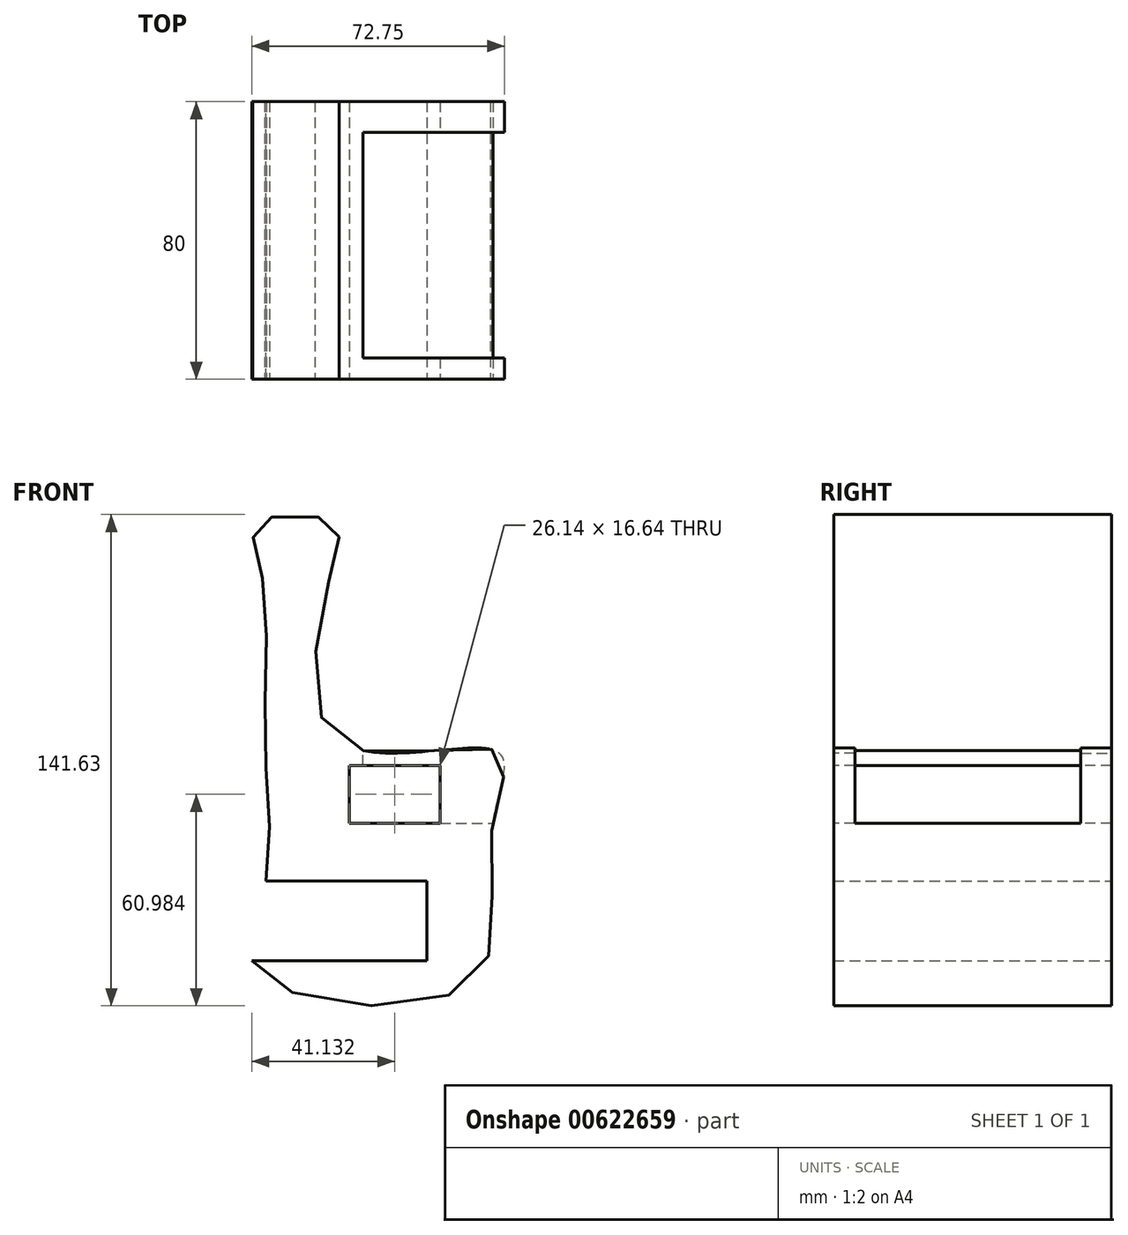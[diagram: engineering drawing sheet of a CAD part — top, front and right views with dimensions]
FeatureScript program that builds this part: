
annotation { "Feature Type Name" : "Feature", "Feature Type Description" : "" }
export const myFeature = defineFeature(function(context is Context, id is Id, definition is map)
    precondition{}
    {
        {
            var Q0;
            Q0=qCreatedBy(makeId("Front.planeOp"),FACE);
            var sketch = newSketch(context, id + "F0", { "sketchPlane" : qUnion([Q0])});
            skFitSpline(sketch, "E0", {"points": [v(-39.55, 48.72) * mm, v(-38.53, 0) * mm, v(-38.53, -41.59) * mm, v(-39.9, -67.05) * mm, v(20.54, -69.77) * mm, v(26.65, -27) * mm, v(28.35, -2.89) * mm, v(-17.14, 0) * mm, v(-19.52, 48.38) * mm, v(-19.52, 63.32) * mm, v(-40.57, 62.98) * mm, v(-39.55, 48.72) * mm]});
            skSolve(sketch);
        }
        {
            var Q0;
            Q0=makeQuery(id+"F0.imprint","IMPRINT",FACE,{"disambiguationData":[TD([[makeQuery(id+"F0.imprint","IMPRINT",EDGE,{"derivedFrom":sQuery(id+"F0.wireOp",EDGE,"E0")}),1.0]])]});
            extrude(context, id + "F1", {"entities" : qUnion([Q0]), "depth" : 80 * mm, "offsetDistance" : 25 * mm});
        }
        {
            var Q0;
            Q0=makeQuery(id+"F1.opExtrude","CAP_FACE",FACE,{"disambiguationData":[OSD([sQuery(id+"F0.wireOp",EDGE,"E0")])],"isStart":false});
            var sketch = newSketch(context, id + "F2", { "sketchPlane" : qUnion([Q0])});
            skLineSegment(sketch, "E1.bottom", {"start": v(-54.62, -40.25) * mm, "end": v(8.16, -40.25) * mm});
            skLineSegment(sketch, "E1.top", {"start": v(-54.62, -63.14) * mm, "end": v(8.16, -63.14) * mm});
            skLineSegment(sketch, "E1.left", {"start": v(-54.62, -40.25) * mm, "end": v(-54.62, -63.14) * mm});
            skLineSegment(sketch, "E1.right", {"start": v(8.16, -40.25) * mm, "end": v(8.16, -63.14) * mm});
            skSolve(sketch);
        }
        {
            var Q0;
            Q0 = qSketchRegion(id + "F2", true);
            extrude(context, id + "F3", {"entities" : qUnion([Q0]), "operationType" : NewBodyOperationType.REMOVE, "oppositeDirection" : true, "depth" : 80 * mm, "offsetDistance" : 25 * mm, "hasSecondDirection" : true, "secondDirectionOppositeDirection" : false, "secondDirectionDepth" : 25 * mm});
        }
        {
            var Q0;
            Q0=makeQuery(id+"F1.opExtrude","CAP_FACE",FACE,{"disambiguationData":[OSD([sQuery(id+"F0.wireOp",EDGE,"E0")])],"isStart":false});
            var sketch = newSketch(context, id + "F4", { "sketchPlane" : qUnion([Q0])});
            skLineSegment(sketch, "E2.bottom", {"start": v(-14.25, -6.89) * mm, "end": v(11.9, -6.89) * mm});
            skLineSegment(sketch, "E2.top", {"start": v(-14.25, -23.52) * mm, "end": v(11.9, -23.52) * mm});
            skLineSegment(sketch, "E2.left", {"start": v(-14.25, -6.89) * mm, "end": v(-14.25, -23.52) * mm});
            skLineSegment(sketch, "E2.right", {"start": v(11.9, -6.89) * mm, "end": v(11.9, -23.52) * mm});
            skSolve(sketch);
        }
        {
            var Q0;
            Q0=makeQuery(id+"F4.imprint","IMPRINT",FACE,{"disambiguationData":[TD([[makeQuery(id+"F4.imprint","IMPRINT",EDGE,{"derivedFrom":sQuery(id+"F4.wireOp",EDGE,"E2.bottom")}),-1.0]])]});
            extrude(context, id + "F5", {"entities" : qUnion([Q0]), "operationType" : NewBodyOperationType.REMOVE, "oppositeDirection" : true, "depth" : 80 * mm, "offsetDistance" : 25 * mm, "hasSecondDirection" : true, "secondDirectionOppositeDirection" : false, "secondDirectionDepth" : 25 * mm});
        }
        {
            var Q0;
            Q0=qCreatedBy(makeId("Top.planeOp"),FACE);
            var sketch = newSketch(context, id + "F6", { "sketchPlane" : qUnion([Q0])});
            skLineSegment(sketch, "E3.bottom", {"start": v(-10.32, -73.88) * mm, "end": v(62.51, -73.88) * mm});
            skLineSegment(sketch, "E3.top", {"start": v(-10.32, -8.84) * mm, "end": v(62.51, -8.84) * mm});
            skLineSegment(sketch, "E3.left", {"start": v(-10.32, -73.88) * mm, "end": v(-10.32, -8.84) * mm});
            skLineSegment(sketch, "E3.right", {"start": v(62.51, -73.88) * mm, "end": v(62.51, -8.84) * mm});
            skSolve(sketch);
        }
        {
            var Q0;
            Q0 = qSketchRegion(id + "F6", true);
            var Q1;
            Q1=makeQuery(id+"F5.boolean.opBoolean","COPY",FACE,{"derivedFrom":makeQuery(id+"F5.opExtrude","SWEPT_FACE",FACE,{"disambiguationData":[OSD([sQuery(id+"F4.wireOp",EDGE,"E2.top")])]})});
            extrude(context, id + "F7", {"entities" : qUnion([Q0]), "operationType" : NewBodyOperationType.REMOVE, "endBound" : BoundingType.UP_TO_SURFACE, "oppositeDirection" : true, "depth" : 25 * mm, "endBoundEntityFace" : qUnion([Q1]), "offsetDistance" : 25 * mm});
        }
    });
